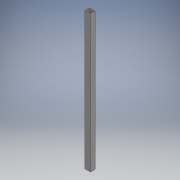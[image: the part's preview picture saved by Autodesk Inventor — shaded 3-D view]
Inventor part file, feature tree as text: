
AUTODESK INVENTOR PART (.ipt)
format: ipt  version: 2016 (Build 200138000, 138)  size: 96,768 bytes
history: native  units: mm
features: extrude x2, sketch x2
ambient origin geometry x8: Origin, YZ Plane, XZ Plane, XY Plane, X Axis, Y Axis, Z Axis, Center Point
bodies: Solid1 (feature_tree)
feature tree (4):
  extrude  "Extrusion1"  Depth=10.0mm
  extrude  "Extrusion3"  Depth=300.0mm TaperAngle=0.0deg
  sketch  "Sketch1"  dims[d0=12.0mm d1=10.0mm]
  sketch  "Sketch3"  dims[d2=300.0mm d3=0.0mm d8=150.0mm d9=0.0mm]
